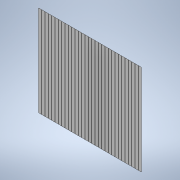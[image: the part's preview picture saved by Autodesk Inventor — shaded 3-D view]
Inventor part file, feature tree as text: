
AUTODESK INVENTOR PART (.ipt)
format: ipt  version: 2021 (Build 250183000, 183)  size: 222,208 bytes
history: native  units: in
note: dims shown in document units (in); Inventor stores cm internally (conversion verified against a paired STEP export)
features: extrude x3, sketch x3, pattern_linear x1, projected_geometry x1
ambient origin geometry x8: Origin, YZ Plane, XZ Plane, XY Plane, X Axis, Y Axis, Z Axis, Center Point
bodies: Solid1 (feature_tree)
feature tree (8):
  extrude  "Extrusion1"  Depth=3.0in
  extrude  "Extrusion2"  Depth=0.1in
  pattern_linear  "Rectangular Pattern1"  Count1=31 Spacing1=0.11in
  extrude  "Extrusion3"  Depth=1.0in TaperAngle=0.0deg
  sketch  "Sketch1"  dims[d0=4.0in d1=3.0in]
  sketch  "Sketch2"  dims[d2=0.04in d3=0.0in d4=0.1in]
  projected_geometry  "Projected Loop1"
  sketch  "Sketch3"  dims[d5=0.0015in d6=0.0in d7=12.2047in d9=0.11in d10=1.0in d11=0.0in]
